# Revit family: CCTYP08
name_source: partatom
category: Furniture
units: mm (PartAtom-declared; Revit-internal decimal feet)

## family parameters
Always vertical = Yes
Cut with Voids When Loaded = No
OmniClass Number = 23.40.20.00
OmniClass Title = General Furniture and Specialties
Render Appearance Source = Family Geometry
Room Calculation Point = No
Shared = No
Work Plane-Based = No

## types (1)
- CCTYP08
    Cost = 17971 $
    Default Elevation = 0 mm  [stored 0 ft]
    Description = 2 x Grafton Side Chair Black Mesh Back/fabric Choice Seat, 1 x Natick Black Configurable Task Chair, 1 x Natick Black Headrest Choice Fabric Field Installed, 1 x 40 Led Task Light, W/ Dimmer & Transformer, 1 x Wall Mounted Overhead w/Cabinet Doors-16Hx66Wx14D, 2 x Pack fee per Chair is less than multiple of 3, 1 x TBL, REC, 2MM, 30DX72WX29H, HAL, E SERIES GLD 2 STAGE, 1 x Cbx Full Depth Floor Bookcase 18dx21hx30w, 1 x Cbx Suspended Hat Modesty 12h For 72w (56 Actual), 1 x Cbx Full Depth Lat Bf 18dx21hx36w, 1 x Cbx Single Door Tower Hinge Left 18dx66hx12w, 1 x Cbx Tackboard Wall Mount 28hx66w
    Exported From CET Designer = Yes
    Manufacturer = AIS
    Model = 4060C
    Show CCTYP08 = Yes
    VisibilityIndex = 0

note: [stored X ft] marks values corroborated as IEEE doubles in the binary element streams (Revit-internal decimal feet)

## geometry (parser evidence)
native form markers: Sweep x3
no freeform markers — native parametric forms only
